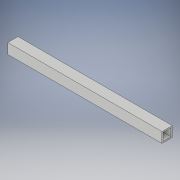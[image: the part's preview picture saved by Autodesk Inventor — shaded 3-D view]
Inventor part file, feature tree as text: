
AUTODESK INVENTOR PART (.ipt)
format: ipt  version: 2018 (Build 220112000, 112)  size: 97,280 bytes
history: native  units: in
note: dims shown in document units (in); Inventor stores cm internally (conversion verified against a paired STEP export)
features: extrude x1, sketch x1
ambient origin geometry x8: Origin, YZ Plane, XZ Plane, XY Plane, X Axis, Y Axis, Z Axis, Center Point
bodies: Solid1 (feature_tree)
feature tree (2):
  extrude  "Extrusion1"  Depth=1.0in
  sketch  "Sketch1"  dims[d0=1.0in d1=1.0in d2=0.125in d3=15.0in d4=0.0in]
